# Revit family: 18-01-010 DN200 Combicross with BL_CAP
name_source: partatom
category: Pipe Accessories
units: mm (PartAtom-declared; Revit-internal decimal feet)

## family parameters
Always vertical = Yes
Cut with Voids When Loaded = No
Part Type = Valve - Breaks Into
Round Connector Dimension = Use Diameter
Shared = No
Work Plane-Based = No

## types (1)
- DN200 With BL_CAP
    1 = 150 mm  [stored 0.492126 ft]
    10 = 10 mm  [stored 0.0328084 ft]
    15 = 15 mm  [stored 0.0492126 ft]
    185 = 185 mm  [stored 0.606955 ft]
    2 = 2 mm  [stored 0.00656168 ft]
    20 = 20 mm  [stored 0.0656168 ft]
    30 = 30 mm  [stored 0.0984252 ft]
    320 = 160 mm  [stored 0.524934 ft]
    40 = 40 mm  [stored 0.131234 ft]
    510 = 255 mm  [stored 0.836614 ft]
    55/2 = 28 mm  [stored 0.0918635 ft]
    Bnt_RR = 140 mm  [stored 0.459318 ft]
    Body_T = 9 mm  [stored 0.0295276 ft]
    Bore = 100 mm  [stored 0.328084 ft]
    C_Bnt_OD = 125 mm  [stored 0.410105 ft]
    C_FL_D = 140 mm  [stored 0.459318 ft]
    C_to_connection = 165 mm  [stored 0.541339 ft]
    Centre_B_H = 203 mm  [stored 0.66601 ft]
    Centre_Bnt_H = 85 mm  [stored 0.278871 ft]
    Centre_Flange_OD = 110 mm  [stored 0.360892 ft]
    Centre_dis = 165 mm  [stored 0.541339 ft]
    Conn.1 = 225 mm  [stored 0.738189 ft]
    Conn.2 = 225 mm  [stored 0.738189 ft]
    Conn.3 = 225 mm  [stored 0.738189 ft]
    DN = 200 mm  [stored 0.656168 ft]
    DN200 With BL_CAP = 18-200-01-FFF894764
    Default Elevation = 0 mm  [stored 0 ft]
    Description_ = COMBI-CROSS, PE PIPE ENDS, PN16
    FL_T = 16 mm  [stored 0.0524934 ft]
    H1 = 195 mm  [stored 0.639764 ft]
    H3 = 685 mm  [stored 2.24738 ft]
    H3-H1 = 490 mm  [stored 1.60761 ft]
    Hole_dia = 13 mm  [stored 0.0426509 ft]
    L = 835 mm
    L3 = 1055 mm  [stored 3.46129 ft]
    L4 = 280 mm  [stored 0.918635 ft]
    PCD = 400 mm  [stored 1.31234 ft]
    Raised_dis = 3 mm  [stored 0.00984252 ft]
    Rib_dim1 = 11 mm  [stored 0.0360892 ft]
    Rib_dim2 = 20 mm  [stored 0.0656168 ft]
    Rib_dim3 = 180 mm  [stored 0.590551 ft]
    Search_table = 18-01-010 DN200 Combicross with BL_CAP
    URL_product_pages = https://www.avkvalves.com
    blind cap = 220 mm  [stored 0.721785 ft]
    test = 100 mm  [stored 0.328084 ft]

note: [stored X ft] marks values corroborated as IEEE doubles in the binary element streams (Revit-internal decimal feet)

## geometry (parser evidence)
native form markers: Sweep x4
no freeform markers — native parametric forms only
